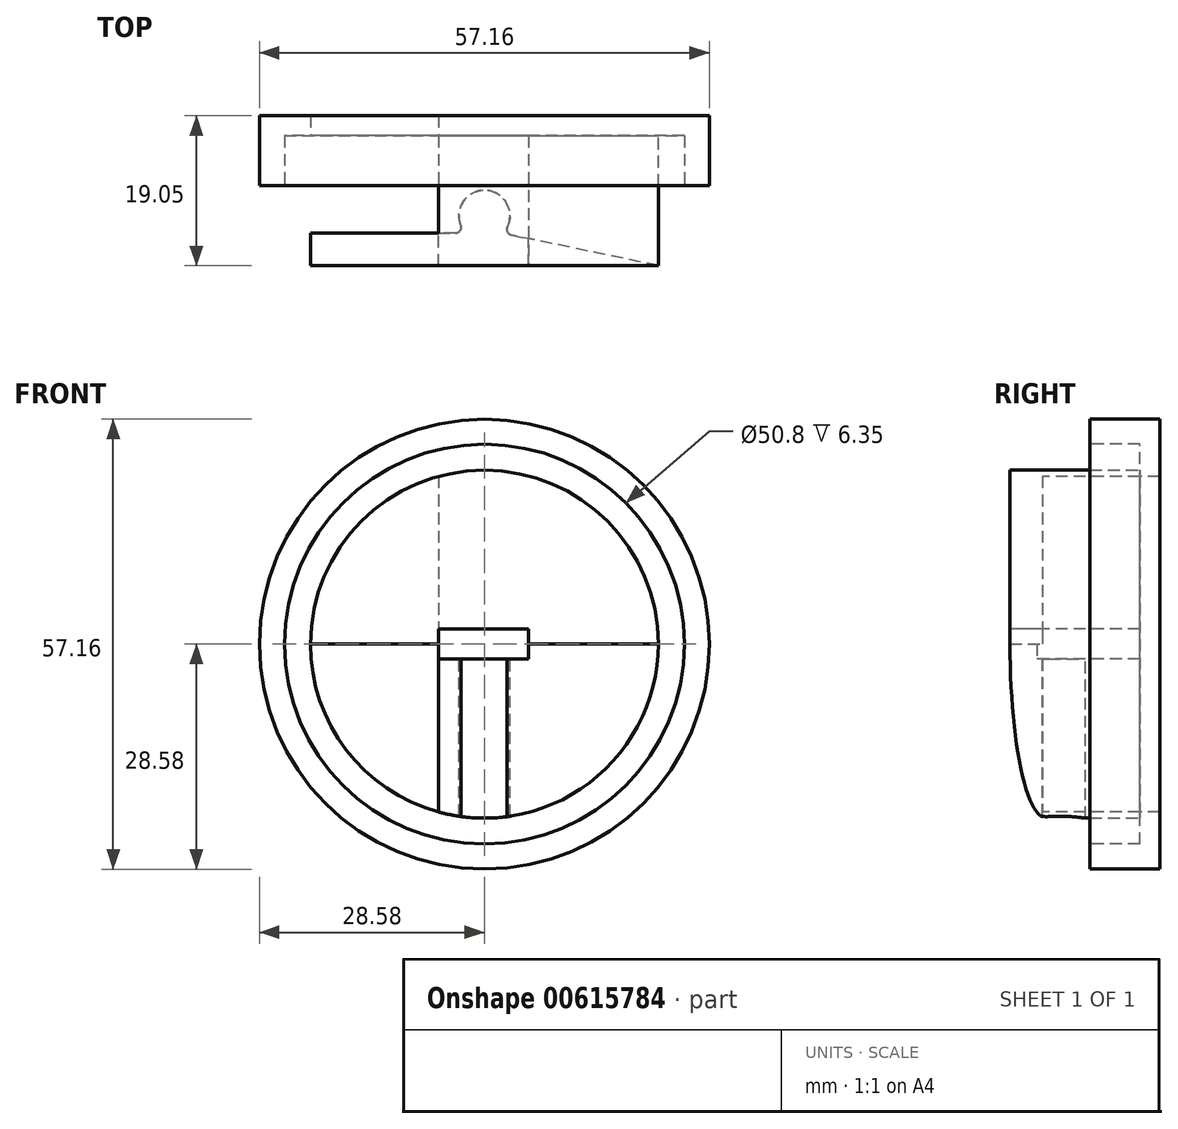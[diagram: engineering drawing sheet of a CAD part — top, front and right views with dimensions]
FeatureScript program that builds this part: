
annotation { "Feature Type Name" : "Feature", "Feature Type Description" : "" }
export const myFeature = defineFeature(function(context is Context, id is Id, definition is map)
    precondition{}
    {
        {
            var Q0;
            Q0=qCreatedBy(makeId("Front.planeOp"),FACE);
            var sketch = newSketch(context, id + "F0", { "sketchPlane" : qUnion([Q0])});
            skCircle(sketch, "E0", {"center": v(0, 0) * mm, "radius": 28.58 * mm});
            skSolve(sketch);
        }
        {
            var Q0;
            Q0 = qSketchRegion(id + "F0", true);
            extrude(context, id + "F1", {"entities" : qUnion([Q0]), "oppositeDirection" : true, "depth" : 8.9 * mm, "offsetDistance" : 25.4 * mm});
        }
        {
            var Q0;
            Q0=makeQuery(id+"F1.opExtrude","CAP_FACE",FACE,{"disambiguationData":[OSD([sQuery(id+"F0.wireOp",EDGE,"E0")])],"isStart":true});
            var sketch = newSketch(context, id + "F2", { "sketchPlane" : qUnion([Q0])});
            skCircle(sketch, "E1", {"center": v(0, 0) * mm, "radius": 25.4 * mm});
            skSolve(sketch);
        }
        {
            var Q0;
            Q0 = qSketchRegion(id + "F2", true);
            extrude(context, id + "F3", {"entities" : qUnion([Q0]), "operationType" : NewBodyOperationType.REMOVE, "oppositeDirection" : true, "depth" : 6.35 * mm, "offsetDistance" : 25.4 * mm});
        }
        {
            var Q0;
            Q0=makeQuery(id+"F1.opExtrude","CAP_FACE",FACE,{"disambiguationData":[OSD([sQuery(id+"F0.wireOp",EDGE,"E0")])],"isStart":true});
            var sketch = newSketch(context, id + "F4", { "sketchPlane" : qUnion([Q0])});
            skCircle(sketch, "E2", {"center": v(0, 0) * mm, "radius": 22.1 * mm});
            skSolve(sketch);
        }
        {
            var Q0;
            Q0 = qSketchRegion(id + "F4", true);
            var Q1;
            Q1=makeQuery(id+"F3.boolean.opBoolean","COPY",FACE,{"derivedFrom":makeQuery(id+"F3.opExtrude","CAP_FACE",FACE,{"disambiguationData":[OSD([sQuery(id+"F2.wireOp",EDGE,"E1")])],"isStart":false})});
            extrude(context, id + "F5", {"entities" : qUnion([Q0]), "operationType" : NewBodyOperationType.ADD, "depth" : 10.16 * mm, "offsetDistance" : 25.4 * mm, "hasSecondDirection" : true, "secondDirectionBound" : SecondDirectionBoundingType.UP_TO_SURFACE, "secondDirectionOppositeDirection" : true, "secondDirectionDepth" : 25.4 * mm, "secondDirectionBoundEntityFace" : qUnion([Q1])});
        }
        {
            var Q0;
            Q0=qCreatedBy(makeId("Top.planeOp"),FACE);
            var sketch = newSketch(context, id + "F6", { "sketchPlane" : qUnion([Q0])});
            skLineSegment(sketch, "E3", {"start": v(22.1, 6.35) * mm, "end": v(22.1, -10.16) * mm, "construction": true});
            skLineSegment(sketch, "E4", {"start": v(22.1, -10.16) * mm, "end": v(2.35, -6.04) * mm});
            skArc(sketch, "E5", {"start": v(2.35, -6.04) * mm, "mid": v(0, -0.57) * mm, "end": v(-2.35, -6.04) * mm});
            skLineSegment(sketch, "E6", {"start": v(3.24, -3.81) * mm, "end": v(-3.24, -3.81) * mm, "construction": true});
            skLineSegment(sketch, "E7", {"start": v(22.1, -10.16) * mm, "end": v(-23.65, -10.16) * mm});
            skLineSegment(sketch, "E8", {"start": v(-2.35, -6.04) * mm, "end": v(-23.65, -6.04) * mm});
            skLineSegment(sketch, "E9", {"start": v(-23.65, -6.04) * mm, "end": v(-23.65, -10.16) * mm});
            skLineSegment(sketch, "E10", {"start": v(2.35, -6.04) * mm, "end": v(-2.35, -6.04) * mm, "construction": true});
            skSolve(sketch);
        }
        {
            var Q0;
            Q0 = qSketchRegion(id + "F6", true);
            var Q1;
            Q1=makeQuery(id+"F5.opExtrude","SWEPT_FACE",FACE,{"disambiguationData":[OSD([sQuery(id+"F4.wireOp",EDGE,"E2")])]});
            var Q2;
            Q2=makeQuery(id+"F5.opExtrude","SWEPT_FACE",FACE,{"disambiguationData":[OSD([sQuery(id+"F4.wireOp",EDGE,"E2")])]});
            extrude(context, id + "F7", {"entities" : qUnion([Q0]), "operationType" : NewBodyOperationType.REMOVE, "endBound" : BoundingType.UP_TO_SURFACE, "oppositeDirection" : true, "depth" : 25.4 * mm, "endBoundEntityFace" : qUnion([Q1]), "offsetDistance" : 25.4 * mm});
        }
        {
            var Q0;
            Q0=makeQuery(id+"F7.boolean.opBoolean","COPY",EDGE,{"derivedFrom":makeQuery(id+"F7.opExtrude","SWEPT_EDGE",EDGE,{"disambiguationData":[OSD([sQuery(id+"F6.wireOp",EDGE,"E5"),sQuery(id+"F6.wireOp",EDGE,"E8")])]})});
            var Q1;
            Q1=makeQuery(id+"F7.boolean.opBoolean","COPY",EDGE,{"derivedFrom":makeQuery(id+"F7.opExtrude","SWEPT_EDGE",EDGE,{"disambiguationData":[OSD([sQuery(id+"F6.wireOp",EDGE,"E4"),sQuery(id+"F6.wireOp",EDGE,"E5")])]})});
            fillet(context, id + "F8", {"entities" : qUnion([Q0, Q1]), "radius" : 0.76 * mm, "tangentPropagation" : true, "allowEdgeOverflow" : false});
        }
        {
            var Q0;
            {var subQ0=sQuery(id+"F6.wireOp",EDGE,"E8");Q0=makeQuery(id+"FPZOFjR6EBKLcpw_1.1.F7.boolean.opBoolean","MERGE",FACE,{"derivedFrom":[makeQuery(id+"F7.boolean.opBoolean","COPY",FACE,{"derivedFrom":makeQuery(id+"F7.opExtrude","SWEPT_FACE",FACE,{"disambiguationData":[OSD([subQ0])]})}),makeQuery(id+"FPZOFjR6EBKLcpw_1.1.F7.opExtrude","SWEPT_FACE",FACE,{"disambiguationData":[OSD([subQ0])]})]});}
            var sketch = newSketch(context, id + "F9", { "sketchPlane" : qUnion([Q0])});
            skLineSegment(sketch, "E11", {"start": v(-5.84, 21.31) * mm, "end": v(-5.84, -21.31) * mm});
            skArc(sketch, "E12", {"start": v(-5.84, 21.31) * mm, "mid": v(-22.1, 0) * mm, "end": v(-5.84, -21.31) * mm});
            skSolve(sketch);
        }
        {
            var Q0;
            Q0 = qSketchRegion(id + "F9", true);
            extrude(context, id + "F10", {"entities" : qUnion([Q0]), "operationType" : NewBodyOperationType.REMOVE, "endBound" : BoundingType.THROUGH_ALL, "oppositeDirection" : true, "depth" : 25.4 * mm, "offsetDistance" : 25.4 * mm});
        }
        {
            var Q0;
            Q0=qCreatedBy(makeId("Front.planeOp"),FACE);
            var sketch = newSketch(context, id + "F11", { "sketchPlane" : qUnion([Q0])});
            skLineSegment(sketch, "E13.bottom", {"start": v(5.59, -1.9) * mm, "end": v(-5.84, -1.9) * mm});
            skLineSegment(sketch, "E13.top", {"start": v(5.59, 1.9) * mm, "end": v(-5.84, 1.9) * mm});
            skLineSegment(sketch, "E13.left", {"start": v(5.59, -1.9) * mm, "end": v(5.59, 1.9) * mm});
            skLineSegment(sketch, "E13.right", {"start": v(-5.84, -1.9) * mm, "end": v(-5.84, 1.9) * mm});
            skPoint(sketch, "E13.middle", {"position": v(-0.13, 0) * mm});
            skSolve(sketch);
        }
        {
            var Q0;
            Q0 = qSketchRegion(id + "F11", true);
            extrude(context, id + "F12", {"entities" : qUnion([Q0]), "operationType" : NewBodyOperationType.REMOVE, "oppositeDirection" : true, "depth" : 6.35 * mm, "offsetDistance" : 25.4 * mm, "hasSecondDirection" : true, "secondDirectionBound" : SecondDirectionBoundingType.THROUGH_ALL, "secondDirectionOppositeDirection" : false, "secondDirectionDepth" : 25.4 * mm});
        }
    });
